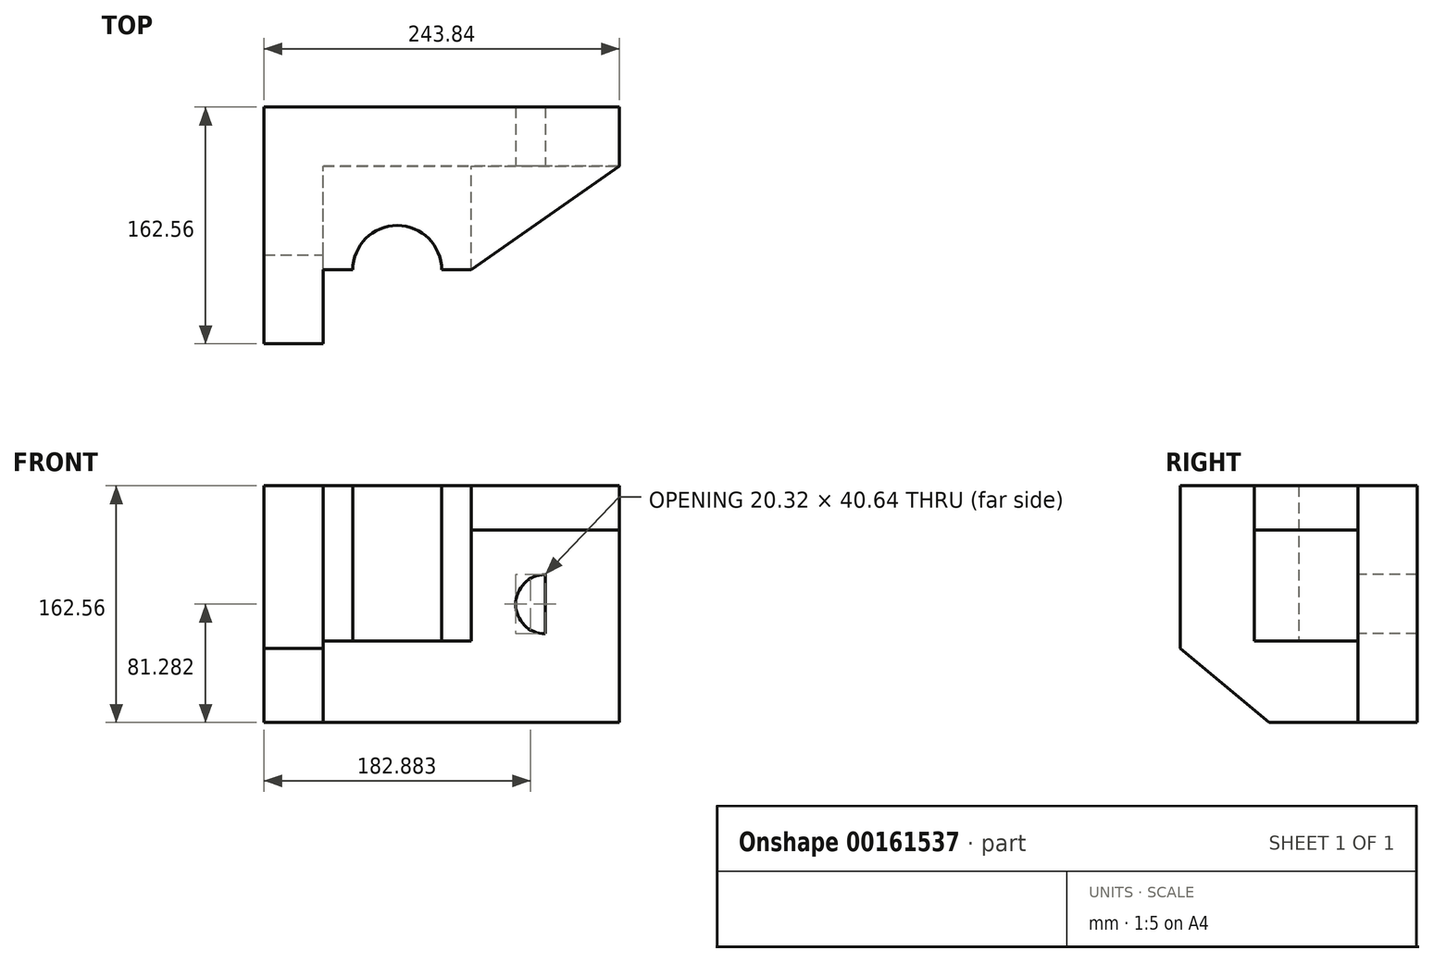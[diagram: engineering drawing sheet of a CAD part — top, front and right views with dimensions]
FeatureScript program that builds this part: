
annotation { "Feature Type Name" : "Feature", "Feature Type Description" : "" }
export const myFeature = defineFeature(function(context is Context, id is Id, definition is map)
    precondition{}
    {
        {
            var Q0;
            Q0=qCreatedBy(makeId("Front.planeOp"),FACE);
            var sketch = newSketch(context, id + "F10", { "sketchPlane" : qUnion([Q0])});
            skLineSegment(sketch, "E0.bottom", {"start": v(121, -104.09) * mm, "end": v(-122.84, -104.09) * mm});
            skLineSegment(sketch, "E0.top", {"start": v(121, 58.47) * mm, "end": v(-122.84, 58.47) * mm});
            skLineSegment(sketch, "E0.left", {"start": v(121, -104.09) * mm, "end": v(121, 58.47) * mm});
            skLineSegment(sketch, "E0.right", {"start": v(-122.84, -104.09) * mm, "end": v(-122.84, 58.47) * mm});
            skPoint(sketch, "E0.middle", {"position": v(-0.92, -22.8) * mm});
            skSolve(sketch);
        }
        {
            var Q0;
            Q0 = qSketchRegion(id + "F10", true);
            extrude(context, id + "F11", {"entities" : qUnion([Q0]), "oppositeDirection" : true, "depth" : 40.64 * mm});
        }
        {
            var Q0;
            Q0=makeQuery(id+"F11.opExtrude","CAP_FACE",FACE,{"disambiguationData":[OSD([sQuery(id+"F10.wireOp",EDGE,"E0.bottom"),sQuery(id+"F10.wireOp",EDGE,"E0.top"),sQuery(id+"F10.wireOp",EDGE,"E0.left"),sQuery(id+"F10.wireOp",EDGE,"E0.right")])],"isStart":true});
            var sketch = newSketch(context, id + "F0", { "sketchPlane" : qUnion([Q0])});
            skLineSegment(sketch, "E1.bottom", {"start": v(-122.84, 58.47) * mm, "end": v(-82.2, 58.47) * mm});
            skLineSegment(sketch, "E1.top", {"start": v(-122.84, -104.09) * mm, "end": v(-82.2, -104.09) * mm});
            skLineSegment(sketch, "E1.left", {"start": v(-122.84, 58.47) * mm, "end": v(-122.84, -104.09) * mm});
            skLineSegment(sketch, "E1.right", {"start": v(-82.2, 58.47) * mm, "end": v(-82.2, -104.09) * mm});
            skLineSegment(sketch, "E2.bottom", {"start": v(-82.2, 58.47) * mm, "end": v(121, 58.47) * mm});
            skLineSegment(sketch, "E2.top", {"start": v(-82.2, 28) * mm, "end": v(121, 28) * mm});
            skLineSegment(sketch, "E2.left", {"start": v(-82.2, 58.47) * mm, "end": v(-82.2, 28) * mm});
            skLineSegment(sketch, "E2.right", {"start": v(121, 58.47) * mm, "end": v(121, 28) * mm});
            skSolve(sketch);
        }
        {
            var Q0;
            Q0=makeQuery(id+"F0.imprint","IMPRINT",FACE,{"disambiguationData":[TD([[makeQuery(id+"F0.imprint","IMPRINT",EDGE,{"derivedFrom":sQuery(id+"F0.wireOp",EDGE,"E1.bottom")}),1.0]])]});
            var sketch = newSketch(context, id + "F1", { "sketchPlane" : qUnion([Q0])});
            skSolve(sketch);
        }
        {
            var Q0;
            Q0=makeQuery(id+"F1.imprint","IMPRINT",FACE,{"disambiguationData":[TD([[makeQuery(id+"F1.imprint","IMPRINT",EDGE,{"derivedFrom":makeQuery(id+"F0.imprint","IMPRINT",EDGE,{"derivedFrom":sQuery(id+"F0.wireOp",EDGE,"E1.bottom")})}),1.0]])]});
            extrude(context, id + "F2", {"entities" : qUnion([Q0]), "operationType" : NewBodyOperationType.ADD, "depth" : 121.92 * mm});
        }
        {
            var Q0;
            Q0=makeQuery(id+"F0.imprint","IMPRINT",FACE,{"disambiguationData":[TD([[makeQuery(id+"F0.imprint","IMPRINT",EDGE,{"derivedFrom":sQuery(id+"F0.wireOp",EDGE,"E2.bottom")}),1.0]])]});
            extrude(context, id + "F12", {"entities" : qUnion([Q0]), "operationType" : NewBodyOperationType.ADD, "depth" : 71.12 * mm});
        }
        {
            var Q0;
            Q0=makeQuery(id+"F11.opExtrude","CAP_FACE",FACE,{"disambiguationData":[OSD([sQuery(id+"F10.wireOp",EDGE,"E0.bottom"),sQuery(id+"F10.wireOp",EDGE,"E0.top"),sQuery(id+"F10.wireOp",EDGE,"E0.left"),sQuery(id+"F10.wireOp",EDGE,"E0.right")])],"isStart":true});
            var sketch = newSketch(context, id + "F3", { "sketchPlane" : qUnion([Q0])});
            skLineSegment(sketch, "E3.bottom", {"start": v(-82.2, 28) * mm, "end": v(19.4, 28) * mm});
            skLineSegment(sketch, "E3.top", {"start": v(-82.2, -48.2) * mm, "end": v(19.4, -48.2) * mm});
            skLineSegment(sketch, "E3.left", {"start": v(-82.2, 28) * mm, "end": v(-82.2, -48.2) * mm});
            skLineSegment(sketch, "E3.right", {"start": v(19.4, 28) * mm, "end": v(19.4, -48.2) * mm});
            skSolve(sketch);
        }
        {
            var Q0;
            Q0=makeQuery(id+"F3.imprint","IMPRINT",FACE,{"disambiguationData":[TD([[makeQuery(id+"F3.imprint","IMPRINT",EDGE,{"derivedFrom":sQuery(id+"F3.wireOp",EDGE,"E3.bottom")}),-1.0]])]});
            extrude(context, id + "F4", {"entities" : qUnion([Q0]), "operationType" : NewBodyOperationType.ADD, "depth" : 71.12 * mm});
        }
        {
            var Q0;
            Q0=makeQuery(id+"F11.opExtrude","CAP_FACE",FACE,{"disambiguationData":[OSD([sQuery(id+"F10.wireOp",EDGE,"E0.bottom"),sQuery(id+"F10.wireOp",EDGE,"E0.top"),sQuery(id+"F10.wireOp",EDGE,"E0.left"),sQuery(id+"F10.wireOp",EDGE,"E0.right")])],"isStart":true});
            var sketch = newSketch(context, id + "F5", { "sketchPlane" : qUnion([Q0])});
            skLineSegment(sketch, "E4.bottom", {"start": v(121, 28) * mm, "end": v(121, 28) * mm});
            skLineSegment(sketch, "E4.top", {"start": v(121, 28) * mm, "end": v(121, 28) * mm});
            skLineSegment(sketch, "E4.left", {"start": v(121, 28) * mm, "end": v(121, 28) * mm});
            skLineSegment(sketch, "E4.right", {"start": v(121, 28) * mm, "end": v(121, 28) * mm});
            skLineSegment(sketch, "E5.bottom", {"start": v(121, -104.09) * mm, "end": v(70.2, -104.09) * mm});
            skLineSegment(sketch, "E5.top", {"start": v(121, -43.13) * mm, "end": v(70.2, -43.13) * mm});
            skLineSegment(sketch, "E5.left", {"start": v(121, -104.09) * mm, "end": v(121, -43.13) * mm});
            skLineSegment(sketch, "E5.right", {"start": v(70.2, -104.09) * mm, "end": v(70.2, -43.13) * mm});
            skLineSegment(sketch, "E6.bottom", {"start": v(70.2, -43.13) * mm, "end": v(121, -43.13) * mm});
            skLineSegment(sketch, "E6.top", {"start": v(70.2, -2.49) * mm, "end": v(121, -2.49) * mm});
            skLineSegment(sketch, "E6.left", {"start": v(70.2, -43.13) * mm, "end": v(70.2, -2.49) * mm});
            skLineSegment(sketch, "E6.right", {"start": v(121, -43.13) * mm, "end": v(121, -2.49) * mm});
            skArc(sketch, "E7", {"start": v(70.2, -43.13) * mm, "mid": v(49.88, -22.8) * mm, "end": v(70.2, -2.49) * mm});
            skSolve(sketch);
        }
        {
            var Q0;
            Q0=makeQuery(id+"F5.imprint","IMPRINT",FACE,{"disambiguationData":[TD([[makeQuery(id+"F5.imprint","IMPRINT",EDGE,{"derivedFrom":sQuery(id+"F5.wireOp",EDGE,"E6.left")}),1.0]])]});
            var Q1;
            Q1=makeQuery(id+"F5.imprint","IMPRINT",FACE,{"disambiguationData":[TD([[makeQuery(id+"F5.imprint","IMPRINT",EDGE,{"derivedFrom":sQuery(id+"F5.wireOp",EDGE,"E6.bottom")}),1.0]])]});
            extrude(context, id + "F6", {"entities" : qUnion([Q0, Q1]), "operationType" : NewBodyOperationType.REMOVE, "oppositeDirection" : true, "depth" : 40.64 * mm});
        }
        {
            var Q0;
            Q0=makeQuery(id+"F12.opExtrude","SWEPT_FACE",FACE,{"disambiguationData":[OSD([sQuery(id+"F0.wireOp",EDGE,"E2.top")])]});
            var sketch = newSketch(context, id + "F7", { "sketchPlane" : qUnion([Q0])});
            skLineSegment(sketch, "E8", {"start": v(19.4, 71.12) * mm, "end": v(121, 0) * mm});
            skLineSegment(sketch, "E9", {"start": v(98.7, 54.05) * mm, "end": v(98.7, 54.05) * mm});
            skLineSegment(sketch, "E10", {"start": v(121, 0) * mm, "end": v(121, 71.12) * mm});
            skSolve(sketch);
        }
        {
            var Q0;
            Q0=makeQuery(id+"F7.imprint","IMPRINT",FACE,{"disambiguationData":[TD([[makeQuery(id+"F7.imprint","IMPRINT",EDGE,{"derivedFrom":sQuery(id+"F7.wireOp",EDGE,"E8")}),1.0]])]});
            extrude(context, id + "F8", {"entities" : qUnion([Q0]), "operationType" : NewBodyOperationType.REMOVE, "oppositeDirection" : true, "depth" : 30.48 * mm});
        }
        {
            var Q0;
            Q0=makeQuery(id+"F4.opExtrude","SWEPT_FACE",FACE,{"disambiguationData":[OSD([sQuery(id+"F3.wireOp",EDGE,"E3.top")])]});
            var sketch = newSketch(context, id + "F9", { "sketchPlane" : qUnion([Q0])});
            skCircle(sketch, "E11", {"center": v(-31.4, 71.12) * mm, "radius": 30.48 * mm});
            skSolve(sketch);
        }
        {
            var Q0;
            {var subQ0=sQuery(id+"F9.wireOp",EDGE,"E11");var subQ1=makeQuery(id+"F4.opExtrude","CAP_EDGE",EDGE,{"disambiguationData":[OSD([sQuery(id+"F3.wireOp",EDGE,"E3.top")])],"isStart":false});var subQ2=makeQuery(id+"F9.imprint","INTERSECT",VERTEX,{"disambiguationData":[OD(0.0)],"derivedFrom":[subQ1,subQ0]});Q0=makeQuery(id+"F9.imprint","IMPRINT",FACE,{"disambiguationData":[TD([[makeQuery(id+"F9.imprint","IMPRINT",EDGE,{"disambiguationData":[TD([[subQ2,1.0]])],"derivedFrom":subQ0}),1.0]])]});}
            extrude(context, id + "F13", {"entities" : qUnion([Q0]), "operationType" : NewBodyOperationType.REMOVE, "oppositeDirection" : true, "depth" : 162.56 * mm});
        }
        {
            var Q0;
            Q0=makeQuery(id+"F2.opExtrude","SWEPT_FACE",FACE,{"disambiguationData":[OSD([sQuery(id+"F0.wireOp",EDGE,"E1.right"),sQuery(id+"F0.wireOp",EDGE,"E2.left")])]});
            var sketch = newSketch(context, id + "F14", { "sketchPlane" : qUnion([Q0])});
            skLineSegment(sketch, "E12", {"start": v(-121.92, -53.29) * mm, "end": v(-60.96, -104.09) * mm});
            skLineSegment(sketch, "E13", {"start": v(-60.96, -104.09) * mm, "end": v(-121.92, -104.09) * mm});
            skLineSegment(sketch, "E14", {"start": v(-121.92, -104.09) * mm, "end": v(-121.92, -53.29) * mm});
            skSolve(sketch);
        }
        {
            var Q0;
            Q0=makeQuery(id+"F14.imprint","IMPRINT",FACE,{"disambiguationData":[TD([[makeQuery(id+"F14.imprint","IMPRINT",EDGE,{"derivedFrom":sQuery(id+"F14.wireOp",EDGE,"E12")}),-1.0]])]});
            extrude(context, id + "F15", {"entities" : qUnion([Q0]), "operationType" : NewBodyOperationType.REMOVE, "oppositeDirection" : true, "depth" : 50.8 * mm});
        }
    });
